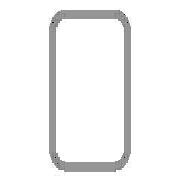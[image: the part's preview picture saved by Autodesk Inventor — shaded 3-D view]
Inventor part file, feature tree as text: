
AUTODESK INVENTOR PART (.ipt)
format: ipt  version: 2025 (Build 290162010, 162A)  size: 153,088 bytes
history: native  units: mm (DEFAULTED — no unit token found)
features: other x4, plane x3, split x2, sketch x1
ambient origin geometry x8: Origin, YZ Plane, XZ Plane, XY Plane, X Axis, Y Axis, Z Axis, Center Point
bodies: Solid1 (feature_tree), Body (feature_tree)
feature tree (10):
  parser-record x1  (decoder bookkeeping rows leaked as tree rows — omitted from the tree; the rows remain in map.json)
  other  "Driven Length"
  other  "Start Plane"
  other  "End Plane"
  plane  "Work Plane4"
  split  "Split1"
  plane  "Work Plane5"
  split  "Split2"
  sketch  "Sketch3"  dims[d3=615.253612mm d4=0.0mm d7=4.0mm d9=20.0mm d11=40.0mm d12=2.0mm d13=-6.618856mm d14=608.634757mm d15=10.0mm d16=20.0mm d17=90.0deg d18=615.253612mm]
  plane  "Work Plane3"
